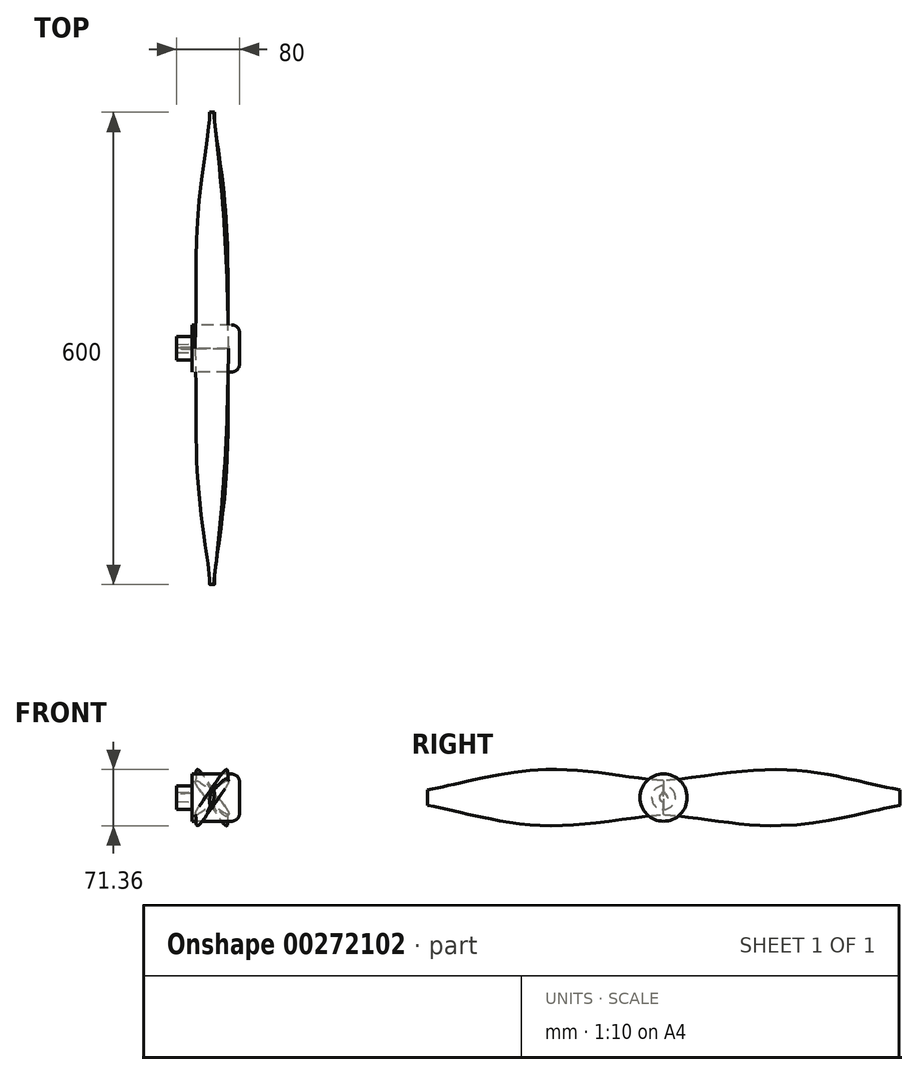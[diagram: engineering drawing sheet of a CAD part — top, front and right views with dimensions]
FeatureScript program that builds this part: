
annotation { "Feature Type Name" : "Feature", "Feature Type Description" : "" }
export const myFeature = defineFeature(function(context is Context, id is Id, definition is map)
    precondition{}
    {
        {
            var Q0;
            Q0=qCreatedBy(makeId("Front.planeOp"),FACE);
            var sketch = newSketch(context, id + "F0", { "sketchPlane" : qUnion([Q0])});
            skEllipse(sketch, "E0", {"center": v(0, 0) * mm, "majorRadius": 30 * mm, "minorRadius": 5 * mm, "majorAxis": v(0.7, 0.7)});
            skLineSegment(sketch, "E1", {"start": v(-3.54, 3.54) * mm, "end": v(3.54, -3.54) * mm, "construction": true});
            skLineSegment(sketch, "E2", {"start": v(-21.21, -21.21) * mm, "end": v(21.21, 21.21) * mm, "construction": true});
            skSolve(sketch);
        }
        {
            assignVariable(context, id + "F1", {"name" : "amplitude", "anyValue" : 300});
        }
        {
            var Q0;
            Q0=qCreatedBy(makeId("Front.planeOp"),FACE);
            cPlane(context, id + "F2", {"entities" : qUnion([Q0]), "cplaneType" : CPlaneType.OFFSET, "offset" : (getVariable(context, 'amplitude') / 2) * mm, "width" : 150 * mm, "height" : 150 * mm});
        }
        {
            var Q0;
            Q0=qCreatedBy(id+"F2.planeOp",FACE);
            var sketch = newSketch(context, id + "F3", { "sketchPlane" : qUnion([Q0])});
            skEllipse(sketch, "E3", {"center": v(0, 0) * mm, "majorRadius": 40 * mm, "minorRadius": 5 * mm, "majorAxis": v(0.46, 0.89)});
            skLineSegment(sketch, "E4", {"start": v(18.47, 35.48) * mm, "end": v(-18.47, -35.48) * mm, "construction": true});
            skLineSegment(sketch, "E5", {"start": v(-4.44, 2.3) * mm, "end": v(4.44, -2.3) * mm, "construction": true});
            skSolve(sketch);
        }
        {
            var Q0;
            Q0=qCreatedBy(makeId("Front.planeOp"),FACE);
            cPlane(context, id + "F4", {"entities" : qUnion([Q0]), "cplaneType" : CPlaneType.OFFSET, "offset" : (getVariable(context, 'amplitude')) * mm, "width" : 150 * mm, "height" : 150 * mm});
        }
        {
            var Q0;
            Q0=qCreatedBy(id+"F4.planeOp",FACE);
            var sketch = newSketch(context, id + "F5", { "sketchPlane" : qUnion([Q0])});
            skEllipse(sketch, "E6", {"center": v(0, 0) * mm, "majorRadius": 10 * mm, "minorRadius": 2.5 * mm, "majorAxis": v(0.17, 0.98)});
            skLineSegment(sketch, "E7", {"start": v(-1.74, -9.85) * mm, "end": v(1.74, 9.85) * mm, "construction": true});
            skLineSegment(sketch, "E8", {"start": v(-2.46, 0.43) * mm, "end": v(2.46, -0.43) * mm, "construction": true});
            skSolve(sketch);
        }
        {
            var Q0;
            Q0 = qSketchRegion(id + "F0", true);
            var Q1;
            Q1 = qSketchRegion(id + "F3", true);
            var Q2;
            Q2 = qSketchRegion(id + "F5", true);
            loft(context, id + "F6", {"sheetProfilesArray" : [{ "sheetProfileEntities" : qUnion([Q0]) }, { "sheetProfileEntities" : qUnion([Q1]) }, { "sheetProfileEntities" : qUnion([Q2]) }]});
        }
        {
            var Q0;
            Q0=qCreatedBy(makeId("Front.planeOp"),FACE);
            var sketch = newSketch(context, id + "F7", { "sketchPlane" : qUnion([Q0])});
            skLineSegment(sketch, "E9", {"start": v(-64.42, 0) * mm, "end": v(60.6, 0) * mm, "construction": true});
            skSolve(sketch);
        }
        {
            var Q0;
            Q0=makeQuery(id+"F6.opLoft","SWEPT_BODY",BODY,{"disambiguationData":[OSD([makeQuery(id+"F0.imprint","IMPRINT",FACE,{"disambiguationData":[TD([[makeQuery(id+"F0.imprint","IMPRINT",EDGE,{"derivedFrom":sQuery(id+"F0.wireOp",EDGE,"E0")}),1.0]])]}),sQuery(id+"F3.wireOp",EDGE,"E3"),makeQuery(id+"F5.imprint","IMPRINT",FACE,{"disambiguationData":[TD([[makeQuery(id+"F5.imprint","IMPRINT",EDGE,{"derivedFrom":sQuery(id+"F5.wireOp",EDGE,"E6")}),1.0]])]})])]});
            var Q1;
            Q1=sQuery(id+"F7.wireOp",EDGE,"E9");
            circularPattern(context, id + "F8", {"entities" : qUnion([Q0]), "axis" : qUnion([Q1]), "angle" : 180 * degree, "instanceCount" : 2, "equalSpace" : true});
        }
        {
            var Q0;
            Q0=qCreatedBy(makeId("Front.planeOp"),FACE);
            var sketch = newSketch(context, id + "F9", { "sketchPlane" : qUnion([Q0])});
            skLineSegment(sketch, "E10", {"start": v(-45, 0) * mm, "end": v(35, 0) * mm});
            skLineSegment(sketch, "E11", {"start": v(35, 0) * mm, "end": v(35, 30) * mm});
            skLineSegment(sketch, "E12", {"start": v(35, 30) * mm, "end": v(-25, 30) * mm});
            skLineSegment(sketch, "E13", {"start": v(-25, 30) * mm, "end": v(-25, 15) * mm});
            skLineSegment(sketch, "E14", {"start": v(-25, 15) * mm, "end": v(-45, 15) * mm});
            skLineSegment(sketch, "E15", {"start": v(-45, 15) * mm, "end": v(-45, 0) * mm});
            skLineSegment(sketch, "E16", {"start": v(-61.67, 0) * mm, "end": v(55.31, 0) * mm, "construction": true});
            skSolve(sketch);
        }
        {
            var Q0;
            Q0 = qSketchRegion(id + "F9", true);
            var Q1;
            Q1=sQuery(id+"F9.wireOp",EDGE,"E16");
            revolve(context, id + "F10", {"entities" : qUnion([Q0]), "axis" : qUnion([Q1]), "revolveType" : RevolveType.FULL});
        }
        {
            var Q0;
            Q0=makeQuery(id+"F10.opRevolve","SWEPT_EDGE",EDGE,{"disambiguationData":[OSD([sQuery(id+"F9.wireOp",EDGE,"E11"),sQuery(id+"F9.wireOp",EDGE,"E12")])]});
            fillet(context, id + "F11", {"entities" : qUnion([Q0]), "radius" : 10 * mm, "tangentPropagation" : true, "allowEdgeOverflow" : false});
        }
        {
            var Q0;
            Q0=makeQuery(id+"F10.opRevolve","SWEPT_FACE",FACE,{"disambiguationData":[OSD([sQuery(id+"F9.wireOp",EDGE,"E15")])]});
            var sketch = newSketch(context, id + "F12", { "sketchPlane" : qUnion([Q0])});
            skArc(sketch, "E17", {"start": v(-1, 4.9) * mm, "mid": v(0, -5) * mm, "end": v(1, 4.9) * mm});
            skLineSegment(sketch, "E18.bottom", {"start": v(-1, 6.9) * mm, "end": v(1, 6.9) * mm});
            skLineSegment(sketch, "E18.left", {"start": v(-1, 6.9) * mm, "end": v(-1, 4.9) * mm});
            skLineSegment(sketch, "E18.right", {"start": v(1, 6.9) * mm, "end": v(1, 4.9) * mm});
            skSolve(sketch);
        }
        {
            var Q0;
            Q0 = qSketchRegion(id + "F12", true);
            extrude(context, id + "F13", {"entities" : qUnion([Q0]), "operationType" : NewBodyOperationType.REMOVE, "oppositeDirection" : true, "depth" : 20 * mm, "hasDraft" : true, "draftAngle" : 1 * degree});
        }
    });
